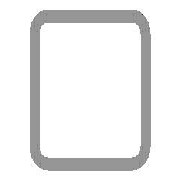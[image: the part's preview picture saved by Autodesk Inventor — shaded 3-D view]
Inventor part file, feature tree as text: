
AUTODESK INVENTOR PART (.ipt)
format: ipt  version: 2025.1 (Build 291241020, 241B)  size: 145,408 bytes
history: native  units: mm (DEFAULTED — no unit token found)
features: other x4, sketch x1, plane x1
ambient origin geometry x8: Origin, YZ Plane, XZ Plane, XY Plane, X Axis, Y Axis, Z Axis, Center Point
bodies: Solid1 (feature_tree), Body (feature_tree)
feature tree (6):
  parser-record x1  (decoder bookkeeping rows leaked as tree rows — omitted from the tree; the rows remain in map.json)
  other  "Driven Length"
  other  "Start plane"
  other  "End plane"
  sketch  "Sketch3"  dims[d3=1050.0mm d4=0.0mm d7=6.0mm d9=100.0mm d11=100.0mm d12=3.0mm d13=100.0mm d14=1150.0mm d15=50.0mm d16=50.0mm d17=90.0deg d18=1050.0mm]
  plane  "Work Plane3"
